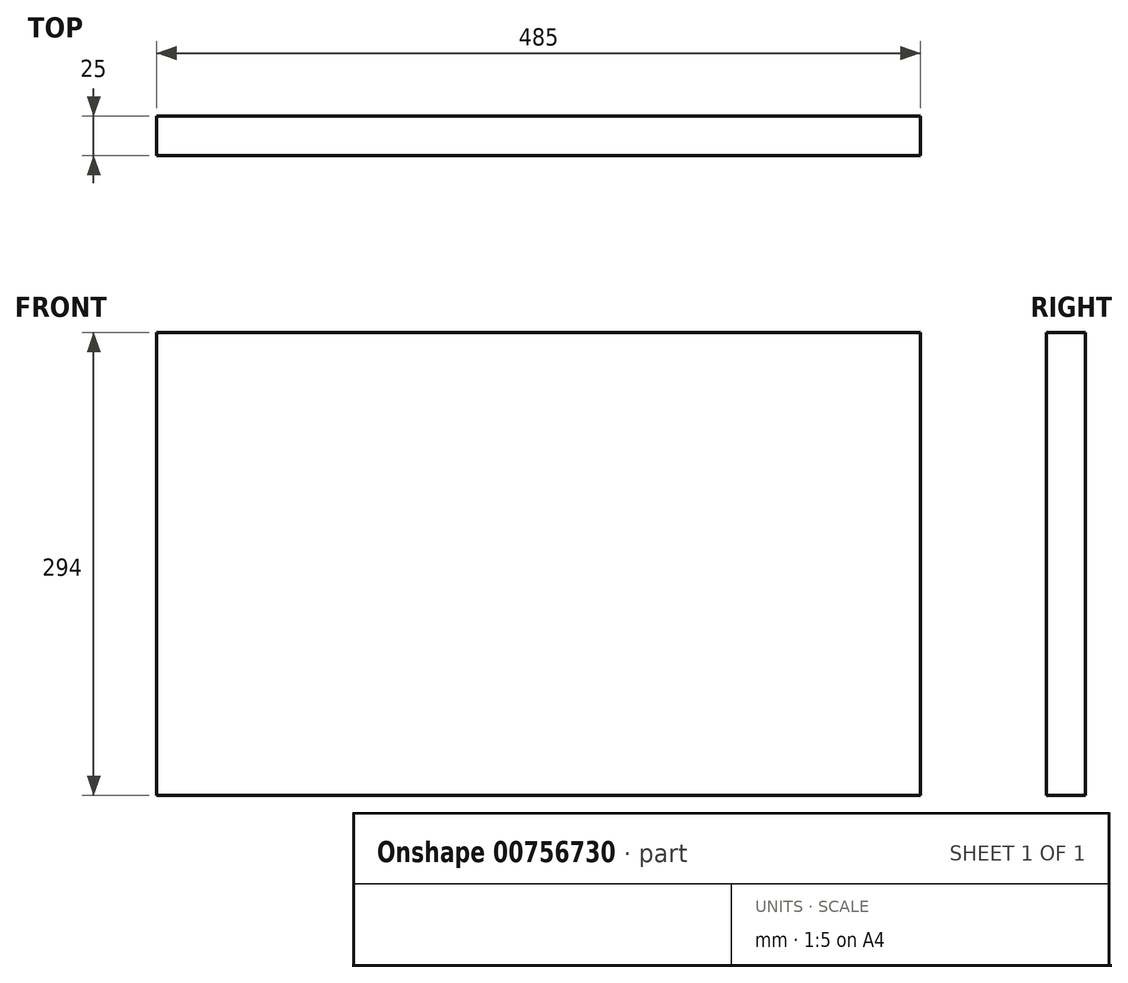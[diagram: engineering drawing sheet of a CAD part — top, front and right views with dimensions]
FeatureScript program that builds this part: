
annotation { "Feature Type Name" : "Feature", "Feature Type Description" : "" }
export const myFeature = defineFeature(function(context is Context, id is Id, definition is map)
    precondition{}
    {
        {
            var Q0;
            Q0=qCreatedBy(makeId("Front.planeOp"),FACE);
            var sketch = newSketch(context, id + "F0", { "sketchPlane" : qUnion([Q0])});
            skLineSegment(sketch, "E0.bottom", {"start": v(-242.5, 294) * mm, "end": v(242.5, 294) * mm});
            skLineSegment(sketch, "E0.top", {"start": v(-242.5, 0) * mm, "end": v(242.5, 0) * mm});
            skLineSegment(sketch, "E0.left", {"start": v(-242.5, 294) * mm, "end": v(-242.5, 0) * mm});
            skLineSegment(sketch, "E0.right", {"start": v(242.5, 294) * mm, "end": v(242.5, 0) * mm});
            skSolve(sketch);
        }
        {
            var Q0;
            Q0 = qSketchRegion(id + "F0", true);
            extrude(context, id + "F1", {"entities" : qUnion([Q0]), "depth" : 25 * mm, "offsetDistance" : 25 * mm});
        }
    });
